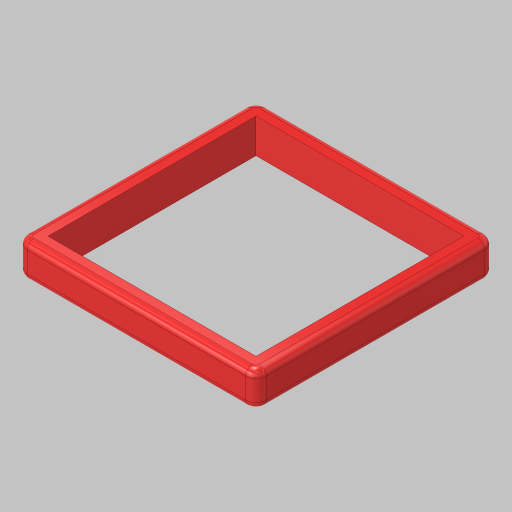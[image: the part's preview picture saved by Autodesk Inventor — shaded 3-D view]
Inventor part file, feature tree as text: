
AUTODESK INVENTOR PART (.ipt)
format: ipt  version: 2023.5 (Build 275446000, 446)  size: 166,912 bytes
history: native  units: in
note: dims shown in document units (in); Inventor stores cm internally (conversion verified against a paired STEP export)
features: fillet x2, extrude x1, sketch x1
ambient origin geometry x8: Origin, YZ Plane, XZ Plane, XY Plane, X Axis, Y Axis, Z Axis, Center Point
bodies: Solid1 (feature_tree)
feature tree (4):
  extrude  "Extrusion1"  Depth=30.25in
  fillet  "Fillet1"  Radius=2.25in
  fillet  "Fillet2"  Radius=5.0in
  sketch  "Sketch1"  dims[d0=30.25in d1=30.25in d2=2.25in d3=5.0in d4=0.0in d5=1.5in d6=1.0in]
